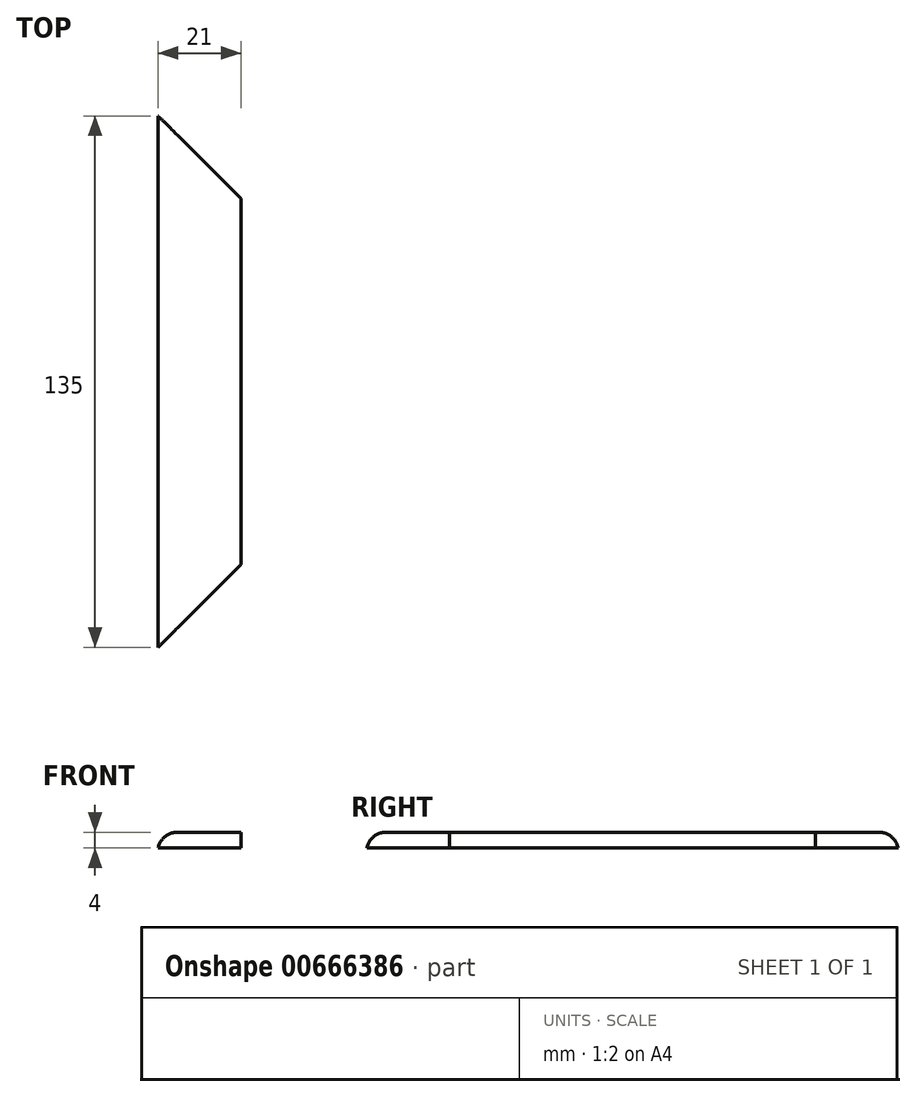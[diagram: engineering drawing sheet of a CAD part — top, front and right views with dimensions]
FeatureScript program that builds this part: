
annotation { "Feature Type Name" : "Feature", "Feature Type Description" : "" }
export const myFeature = defineFeature(function(context is Context, id is Id, definition is map)
    precondition{}
    {
        {
            var Q0;
            Q0=qCreatedBy(makeId("Top.planeOp"),FACE);
            var sketch = newSketch(context, id + "F0", { "sketchPlane" : qUnion([Q0])});
            skLineSegment(sketch, "E0.bottom", {"start": v(10.5, 67.5) * mm, "end": v(-10.5, 67.5) * mm});
            skLineSegment(sketch, "E0.top", {"start": v(10.5, -67.5) * mm, "end": v(-10.5, -67.5) * mm});
            skLineSegment(sketch, "E0.left", {"start": v(10.5, 67.5) * mm, "end": v(10.5, -67.5) * mm});
            skLineSegment(sketch, "E0.right", {"start": v(-10.5, 67.5) * mm, "end": v(-10.5, -67.5) * mm});
            skPoint(sketch, "E0.middle", {"position": v(0, 0) * mm});
            skSolve(sketch);
        }
        {
            var Q0;
            Q0=qSketchRegion(id+"F0",true);
            extrude(context, id + "F1", {"entities" : qUnion([Q0]), "depth" : 4 * mm, "offsetDistance" : 25 * mm});
        }
        {
            var Q0;
            Q0=makeQuery(id+"F1.opExtrude","CAP_FACE",FACE,{"disambiguationData":[OSD([sQuery(id+"F0.wireOp",EDGE,"E0.bottom"),sQuery(id+"F0.wireOp",EDGE,"E0.top"),sQuery(id+"F0.wireOp",EDGE,"E0.left"),sQuery(id+"F0.wireOp",EDGE,"E0.right")])],"isStart":false});
            var sketch = newSketch(context, id + "F2", { "sketchPlane" : qUnion([Q0])});
            skLineSegment(sketch, "E1", {"start": v(-10.5, 67.5) * mm, "end": v(10.5, 46.5) * mm});
            skLineSegment(sketch, "E2", {"start": v(10.5, 46.5) * mm, "end": v(10.5, 67.5) * mm});
            skLineSegment(sketch, "E3", {"start": v(10.5, 67.5) * mm, "end": v(-10.5, 67.5) * mm});
            skLineSegment(sketch, "E4", {"start": v(-10.5, -67.5) * mm, "end": v(10.5, -46.5) * mm});
            skLineSegment(sketch, "E5", {"start": v(10.5, -46.5) * mm, "end": v(10.5, -67.5) * mm});
            skLineSegment(sketch, "E6", {"start": v(10.5, -67.5) * mm, "end": v(-10.5, -67.5) * mm});
            skSolve(sketch);
        }
        {
            var Q0;
            Q0=qSketchRegion(id+"F2",true);
            extrude(context, id + "F3", {"entities" : qUnion([Q0]), "operationType" : NewBodyOperationType.REMOVE, "endBound" : BoundingType.THROUGH_ALL, "oppositeDirection" : true, "depth" : 25 * mm, "offsetDistance" : 25 * mm});
        }
        {
            var Q0;
            Q0=makeQuery(id+"F1.opExtrude","CAP_EDGE",EDGE,{"disambiguationData":[OSD([sQuery(id+"F0.wireOp",EDGE,"E0.right")])],"isStart":false});
            fillet(context, id + "F4", {"entities" : qUnion([Q0]), "radius" : 5 * mm, "tangentPropagation" : true, "allowEdgeOverflow" : false});
        }
    });
